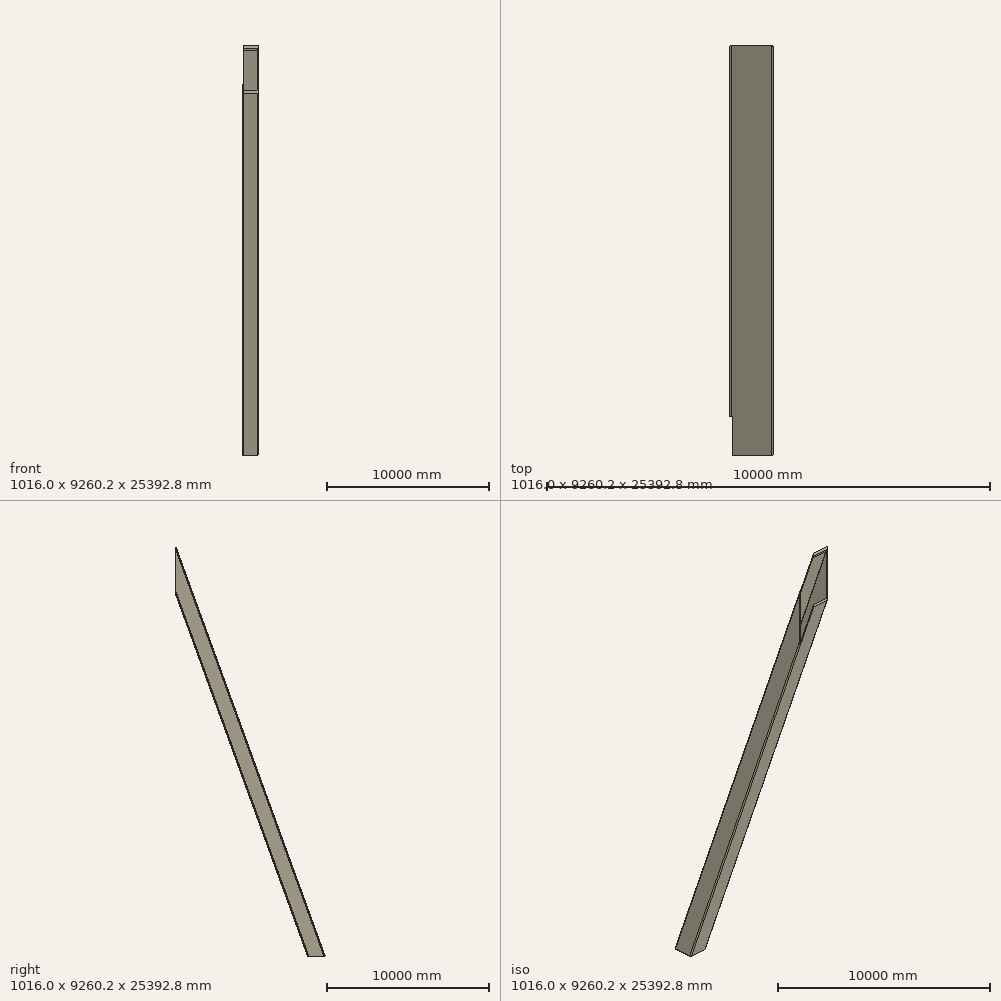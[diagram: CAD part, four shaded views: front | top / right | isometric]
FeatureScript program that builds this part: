
annotation { "Feature Type Name" : "Feature", "Feature Type Description" : "" }
export const myFeature = defineFeature(function(context is Context, id is Id, definition is map)
    precondition{}
    {
        {
            var Q0;
            Q0=qCreatedBy(makeId("Right.planeOp"),FACE);
            var sketch = newSketch(context, id + "F0", { "sketchPlane" : qUnion([Q0])});
            skLineSegment(sketch, "E0", {"start": v(0, 0) * mm, "end": v(-9260.2, 25392.81) * mm});
            skLineSegment(sketch, "E1", {"start": v(-9260.2, 25392.81) * mm, "end": v(-9260.2, 22427.32) * mm});
            skLineSegment(sketch, "E2", {"start": v(-9260.2, 22427.32) * mm, "end": v(-1081.45, 0) * mm});
            skLineSegment(sketch, "E3", {"start": v(-1081.45, 0) * mm, "end": v(0, 0) * mm});
            skSolve(sketch);
        }
        {
            var Q0;
            Q0=makeQuery(id+"F0.imprint","IMPRINT",FACE,{"disambiguationData":[TD([[makeQuery(id+"F0.imprint","IMPRINT",EDGE,{"derivedFrom":sQuery(id+"F0.wireOp",EDGE,"E0")}),1.0]])]});
            extrude(context, id + "F1", {"entities" : qUnion([Q0]), "depth" : 1016 * mm, "offsetDistance" : 25.4 * mm});
        }
        {
            var Q0;
            Q0=makeQuery(id+"F1.opExtrude","CAP_EDGE",EDGE,{"disambiguationData":[OSD([sQuery(id+"F0.wireOp",EDGE,"E2")])],"isStart":true});
            var Q1;
            Q1=makeQuery(id+"F1.opExtrude","CAP_EDGE",EDGE,{"disambiguationData":[OSD([sQuery(id+"F0.wireOp",EDGE,"E2")])],"isStart":false});
            var Q2;
            Q2=makeQuery(id+"F1.opExtrude","CAP_EDGE",EDGE,{"disambiguationData":[OSD([sQuery(id+"F0.wireOp",EDGE,"E0")])],"isStart":true});
            var Q3;
            Q3=makeQuery(id+"F1.opExtrude","CAP_EDGE",EDGE,{"disambiguationData":[OSD([sQuery(id+"F0.wireOp",EDGE,"E0")])],"isStart":false});
            fillet(context, id + "F2", {"entities" : qUnion([Q0, Q1, Q2, Q3]), "radius" : 63.5 * mm, "tangentPropagation" : true, "allowEdgeOverflow" : false});
        }
        {
            var Q0;
            Q0=makeQuery(id+"F1.opExtrude","SWEPT_FACE",FACE,{"disambiguationData":[OSD([sQuery(id+"F0.wireOp",EDGE,"E3")])]});
            shell(context, id + "F3", {"entities" : qUnion([Q0]), "thickness" : 50.8 * mm});
        }
        {
            var Q0;
            Q0=qCreatedBy(makeId("Top.planeOp"),FACE);
            var sketch = newSketch(context, id + "F4", { "sketchPlane" : qUnion([Q0])});
            skLineSegment(sketch, "E4", {"start": v(-174.16, -8374.97) * mm, "end": v(72.29, -8374.97) * mm});
            skLineSegment(sketch, "E5", {"start": v(72.29, -8374.97) * mm, "end": v(72.29, -9402.92) * mm});
            skLineSegment(sketch, "E6", {"start": v(72.29, -9402.92) * mm, "end": v(-174.16, -9402.92) * mm});
            skLineSegment(sketch, "E7", {"start": v(-174.16, -9402.92) * mm, "end": v(-174.16, -8374.97) * mm});
            skSolve(sketch);
        }
        {
            var Q0;
            Q0 = qSketchRegion(id + "F4", true);
            extrude(context, id + "F5", {"entities" : qUnion([Q0]), "operationType" : NewBodyOperationType.REMOVE, "endBound" : BoundingType.THROUGH_ALL, "depth" : 25.4 * mm, "offsetDistance" : 25.4 * mm});
        }
        {
            var Q0;
            Q0=makeQuery(id+"F5.boolean.opBoolean","COPY",FACE,{"derivedFrom":makeQuery(id+"F5.opExtrude","SWEPT_FACE",FACE,{"disambiguationData":[OSD([sQuery(id+"F4.wireOp",EDGE,"E5")])]})});
            var sketch = newSketch(context, id + "F6", { "sketchPlane" : qUnion([Q0])});
            skLineSegment(sketch, "E8", {"start": v(9209.4, 22436.3) * mm, "end": v(9366.11, 22866) * mm});
            skLineSegment(sketch, "E9", {"start": v(9366.11, 22866) * mm, "end": v(9366.11, 25327.68) * mm});
            skLineSegment(sketch, "E10", {"start": v(9366.11, 25327.68) * mm, "end": v(9279.27, 25268.85) * mm});
            skLineSegment(sketch, "E11", {"start": v(9279.27, 25268.85) * mm, "end": v(9209.4, 25105.24) * mm});
            skLineSegment(sketch, "E12", {"start": v(9209.4, 25105.24) * mm, "end": v(9146.08, 24650.7) * mm});
            skLineSegment(sketch, "E13", {"start": v(9146.08, 24650.7) * mm, "end": v(9078.5, 22436.3) * mm});
            skLineSegment(sketch, "E14", {"start": v(9078.5, 22436.3) * mm, "end": v(9209.4, 22436.3) * mm});
            skSolve(sketch);
        }
        {
            var Q0;
            Q0 = qSketchRegion(id + "F6", true);
            extrude(context, id + "F7", {"entities" : qUnion([Q0]), "operationType" : NewBodyOperationType.REMOVE, "oppositeDirection" : true, "depth" : 889 * mm, "offsetDistance" : 25.4 * mm});
        }
    });
